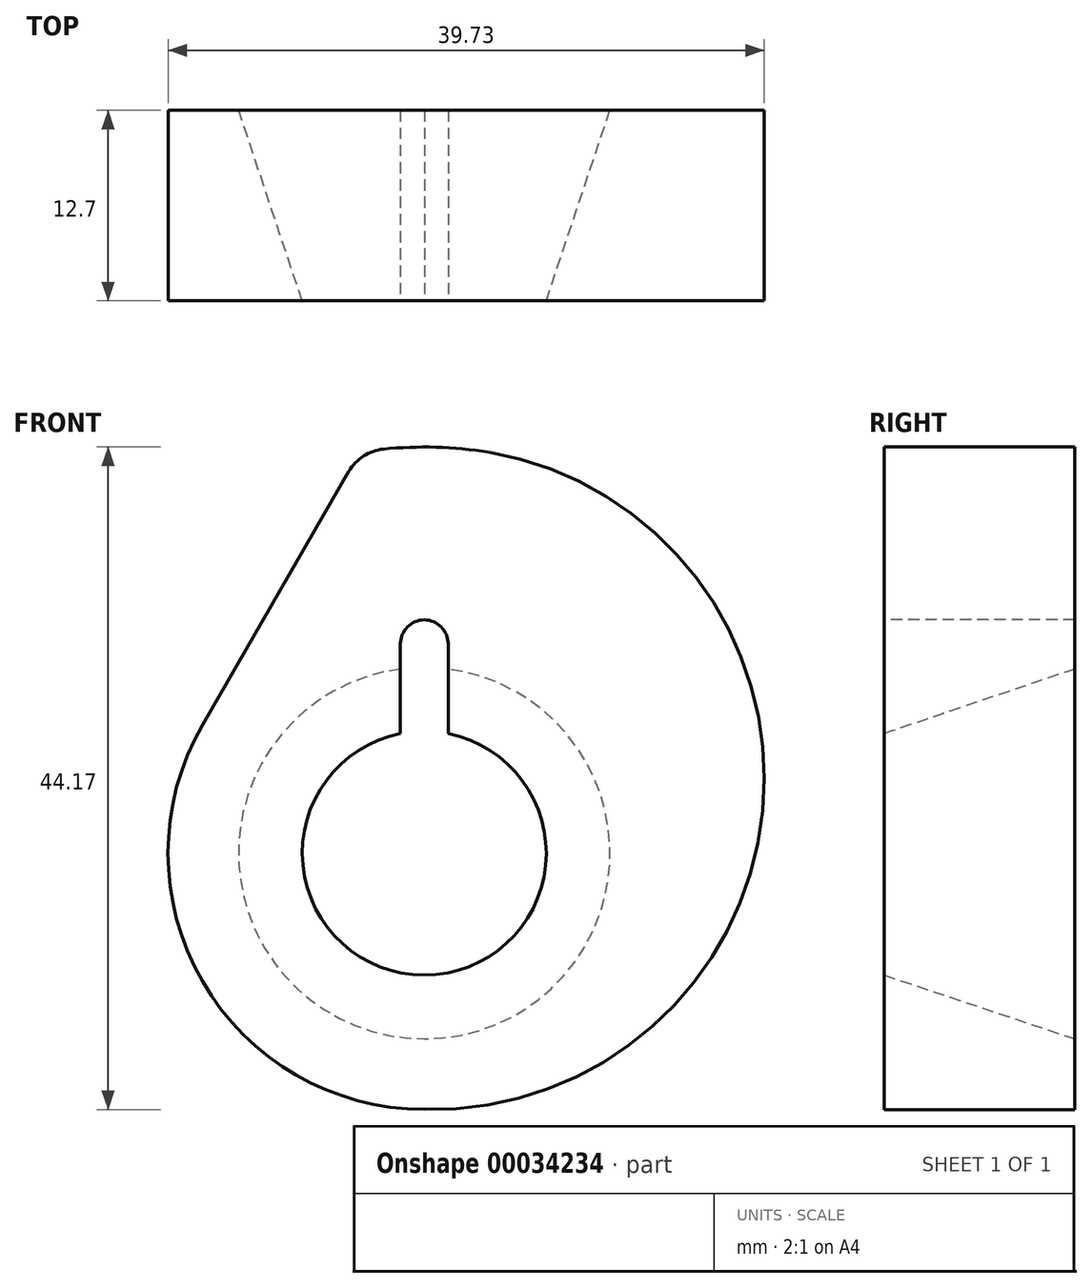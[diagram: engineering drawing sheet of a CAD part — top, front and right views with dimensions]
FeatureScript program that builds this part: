
annotation { "Feature Type Name" : "Feature", "Feature Type Description" : "" }
export const myFeature = defineFeature(function(context is Context, id is Id, definition is map)
    precondition{}
    {
        {
            var Q0;
            Q0=qCreatedBy(makeId("Front.planeOp"),FACE);
            var sketch = newSketch(context, id + "F0", { "sketchPlane" : qUnion([Q0])});
            skLineSegment(sketch, "E0.0.1.0", {"start": v(-14.8, 8.54) * mm, "end": v(-5.03, 25.46) * mm});
            skArc(sketch, "E0.0.1.1", {"start": v(4.28, 26.74) * mm, "mid": v(0.78, 27.07) * mm, "end": v(-2.73, 26.94) * mm});
            skArc(sketch, "E0.0.1.2", {"start": v(-14.8, 8.54) * mm, "mid": v(-14.8, -8.54) * mm, "end": v(0, -17.08) * mm});
            skArc(sketch, "E0.0.1.3", {"start": v(0, -17.08) * mm, "mid": v(22.55, 2.83) * mm, "end": v(4.28, 26.74) * mm});
            skCircle(sketch, "E0.0.1.4", {"center": v(0, 0) * mm, "radius": 8.13 * mm});
            skArc(sketch, "E0.0.1.5", {"start": v(-2.73, 26.94) * mm, "mid": v(-4.06, 26.48) * mm, "end": v(-5.03, 25.46) * mm});
            skSolve(sketch);
        }
        {
            var Q0;
            Q0 = qSketchRegion(id + "F0", true);
            extrude(context, id + "F1", {"entities" : qUnion([Q0]), "oppositeDirection" : true, "depth" : 12.7 * mm});
        }
        {
            var Q0;
            Q0=qCreatedBy(makeId("Top.planeOp"),FACE);
            var sketch = newSketch(context, id + "F2", { "sketchPlane" : qUnion([Q0])});
            skLineSegment(sketch, "E1", {"start": v(8.13, 0) * mm, "end": v(12.46, 12.95) * mm});
            skLineSegment(sketch, "E2", {"start": v(12.46, 12.95) * mm, "end": v(8.13, 12.95) * mm});
            skLineSegment(sketch, "E3.0", {"start": v(1.78, 12.95) * mm, "end": v(1.78, 0) * mm});
            skLineSegment(sketch, "E4", {"start": v(8.13, 0) * mm, "end": v(1.78, 0) * mm});
            skLineSegment(sketch, "E5", {"start": v(8.13, 12.95) * mm, "end": v(1.78, 12.95) * mm});
            skSolve(sketch);
        }
        {
            var Q0;
            Q0 = qSketchRegion(id + "F2", true);
            var Q1;
            Q1=makeQuery(id+"F1.opExtrude","SWEPT_FACE",FACE,{"disambiguationData":[OSD([sQuery(id+"F0.wireOp",EDGE,"E0.0.1.4")])]});
            revolve(context, id + "F3", {"operationType" : NewBodyOperationType.REMOVE, "entities" : qUnion([Q0]), "axis" : qUnion([Q1]), "revolveType" : RevolveType.FULL, "oppositeDirection" : true});
        }
        {
            var Q0;
            Q0=makeQuery(id+"F1.opExtrude","CAP_FACE",FACE,{"disambiguationData":[OSD([sQuery(id+"F0.wireOp",EDGE,"E0.0.1.0"),sQuery(id+"F0.wireOp",EDGE,"E0.0.1.1"),sQuery(id+"F0.wireOp",EDGE,"E0.0.1.2"),sQuery(id+"F0.wireOp",EDGE,"E0.0.1.3"),sQuery(id+"F0.wireOp",EDGE,"E0.0.1.4"),sQuery(id+"F0.wireOp",EDGE,"E0.0.1.5")])],"isStart":true});
            var sketch = newSketch(context, id + "F4", { "sketchPlane" : qUnion([Q0])});
            skLineSegment(sketch, "E6.MirrorCS", {"start": v(-1.59, 3.08) * mm, "end": v(1.59, 3.08) * mm});
            skArc(sketch, "E7", {"start": v(1.59, 13.97) * mm, "mid": v(0, 15.56) * mm, "end": v(-1.59, 13.97) * mm});
            skLineSegment(sketch, "E8.0", {"start": v(-1.59, 3.08) * mm, "end": v(-1.59, 13.97) * mm});
            skLineSegment(sketch, "E9.0", {"start": v(1.59, 3.08) * mm, "end": v(1.59, 13.97) * mm});
            skSolve(sketch);
        }
        {
            var Q0;
            Q0 = qSketchRegion(id + "F4", true);
            extrude(context, id + "F5", {"entities" : qUnion([Q0]), "operationType" : NewBodyOperationType.REMOVE, "endBound" : BoundingType.THROUGH_ALL, "oppositeDirection" : true, "depth" : 25.4 * mm});
        }
    });
